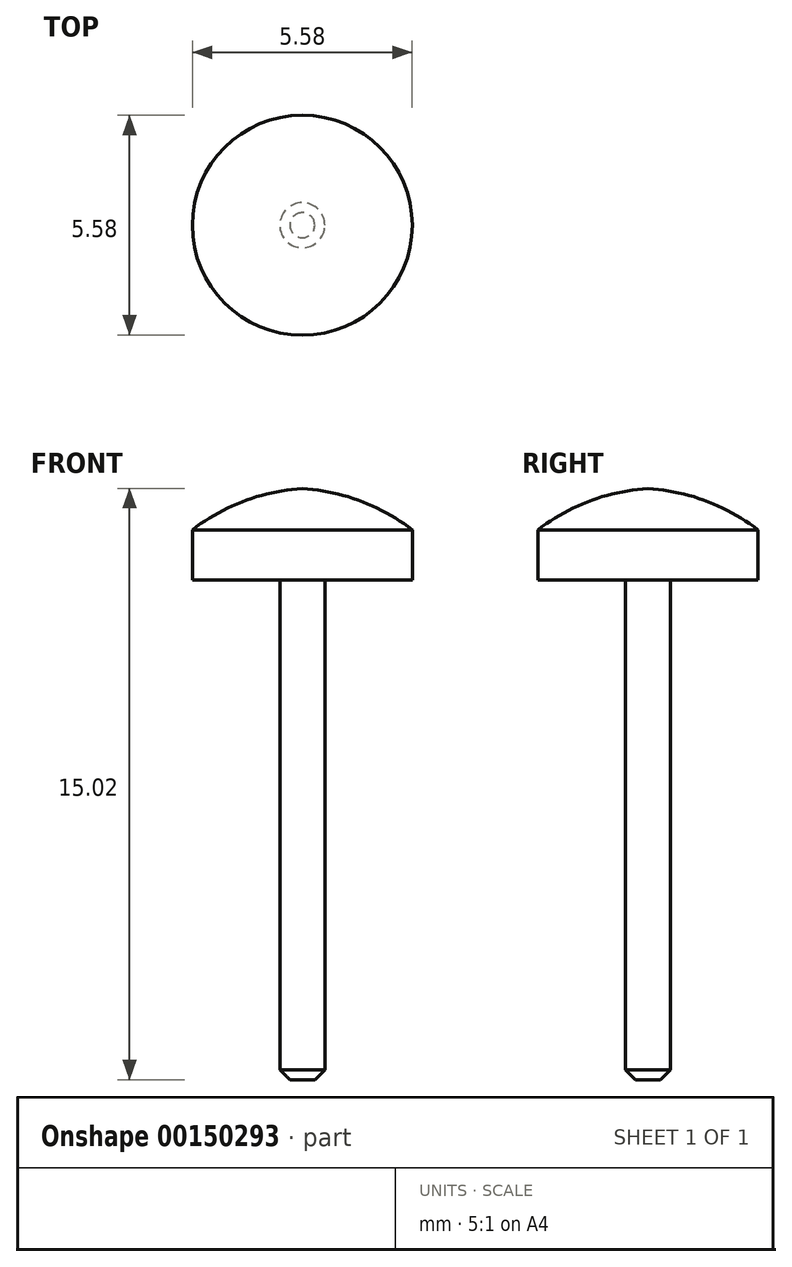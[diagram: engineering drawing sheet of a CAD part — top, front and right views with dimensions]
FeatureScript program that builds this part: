
annotation { "Feature Type Name" : "Feature", "Feature Type Description" : "" }
export const myFeature = defineFeature(function(context is Context, id is Id, definition is map)
    precondition{}
    {
        {
            var Q0;
            Q0=qCreatedBy(makeId("Front.planeOp"),FACE);
            var sketch = newSketch(context, id + "F0", { "sketchPlane" : qUnion([Q0])});
            skLineSegment(sketch, "E0", {"start": v(0, 0) * mm, "end": v(2.8, 0) * mm});
            skArc(sketch, "E1", {"start": v(2.8, 0) * mm, "mid": v(1.48, 0.73) * mm, "end": v(0, 1.05) * mm});
            skLineSegment(sketch, "E2", {"start": v(0, 1.05) * mm, "end": v(0, 0) * mm});
            skSolve(sketch);
        }
        {
            var Q0;
            Q0 = qSketchRegion(id + "F0", true);
            var Q1;
            Q1=sQuery(id+"F0.wireOp",EDGE,"E2");
            revolve(context, id + "F1", {"entities" : qUnion([Q0]), "axis" : qUnion([Q1]), "revolveType" : RevolveType.FULL});
        }
        {
            var Q0;
            Q0=makeQuery(id+"F1.opRevolve","SWEPT_FACE",FACE,{"disambiguationData":[OSD([sQuery(id+"F0.wireOp",EDGE,"E0")])]});
            var sketch = newSketch(context, id + "F2", { "sketchPlane" : qUnion([Q0])});
            skCircle(sketch, "E3", {"center": v(0, 0) * mm, "radius": 2.8 * mm});
            skSolve(sketch);
        }
        {
            var Q0;
            Q0 = qSketchRegion(id + "F2", true);
            extrude(context, id + "F3", {"entities" : qUnion([Q0]), "operationType" : NewBodyOperationType.ADD, "depth" : 1.27 * mm});
        }
        {
            var Q0;
            Q0=makeQuery(id+"F3.opExtrude","CAP_FACE",FACE,{"disambiguationData":[OSD([sQuery(id+"F2.wireOp",EDGE,"E3")])],"isStart":false});
            var sketch = newSketch(context, id + "F4", { "sketchPlane" : qUnion([Q0])});
            skCircle(sketch, "E4", {"center": v(0, 0) * mm, "radius": 0.57 * mm});
            skSolve(sketch);
        }
        {
            var Q0;
            Q0 = qSketchRegion(id + "F4", true);
            extrude(context, id + "F5", {"entities" : qUnion([Q0]), "operationType" : NewBodyOperationType.ADD, "depth" : 12.7 * mm});
        }
        {
            var Q0;
            Q0=makeQuery(id+"F5.opExtrude","CAP_EDGE",EDGE,{"disambiguationData":[OSD([sQuery(id+"F4.wireOp",EDGE,"E4")])],"isStart":false});
            chamfer(context, id + "F6", {"entities" : qUnion([Q0]), "width" : 0.25 * mm, "tangentPropagation" : true});
        }
    });
